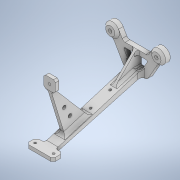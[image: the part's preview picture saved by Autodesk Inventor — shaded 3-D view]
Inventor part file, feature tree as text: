
AUTODESK INVENTOR PART (.ipt)
format: ipt  version: 2020 (Build 240168000, 168)  size: 514,560 bytes
history: native  units: mm
features: extrude x16, sketch x15, projected_geometry x15, fillet x13, reference x6, other x6, plane x3, chamfer x3, thicken_offset x2, mirror x1
ambient origin geometry x8: Origin, YZ Plane, XZ Plane, XY Plane, X Axis, Y Axis, Z Axis, Center Point
bodies: Solid1 (feature_tree)
feature tree (80):
  extrude  "Extrusion1"  Depth=12.0mm
  extrude  "Extrusion2"  Depth=4.0mm
  plane  "Work Plane1"
  extrude  "Extrusion3"  Depth=5.0mm
  extrude  "Extrusion4"  Depth=5.0mm
  sketch  "Sketch5"  dims[d7=10.0mm d8=0.0mm d9=5.0mm]
  plane  "Work Plane2"
  extrude  "Extrusion5"  Depth=2.0mm
  extrude  "Extrusion6"  Depth=4.0mm
  mirror  "Mirror1"
  extrude  "Extrusion7"  Depth=10.0mm TaperAngle=0.0deg
  extrude  "Extrusion8"  Depth=23.0mm
  extrude  "Extrusion9"  Depth=2.0mm
  plane  "Work Plane3"
  extrude  "Extrusion10"  Depth=3.0mm TaperAngle=0.0deg
  extrude  "Extrusion11"  Depth=6.0mm TaperAngle=0.0deg
  fillet  "Fillet1"  Radius=4.0mm
  fillet  "Fillet2"  Radius=4.0mm
  fillet  "Fillet3"  Radius=6.0mm
  chamfer  "Chamfer2"  Distance=2.0mm
  chamfer  "Chamfer3"  Distance=2.0mm
  fillet  "Fillet4"  Radius=5.0mm
  extrude  "Extrusion12"  Depth=3.0mm
  thicken_offset  "Thicken1"
  thicken_offset  "Thicken2"
  fillet  "Fillet5"  Radius=10.0mm
  fillet  "Fillet6"  Radius=10.0mm
  fillet  "Fillet7"  Radius=20.0mm
  fillet  "Fillet8"  Radius=3.0mm
  fillet  "Fillet9"  Radius=2.0mm
  fillet  "Fillet10"  Radius=3.0mm
  fillet  "Fillet11"  Radius=3.0mm
  fillet  "Fillet12"  Radius=2.0mm
  fillet  "Fillet13"  Radius=2.0mm
  extrude  "Extrusion13"  Depth=2.0mm
  extrude  "Extrusion14"  Depth=10.0mm
  extrude  "Extrusion15"  Depth=2.0mm
  extrude  "Extrusion16"  Depth=3.0mm TaperAngle=0.0deg
  chamfer  "Chamfer4"  Distance=2.0mm
  reference  "Reference1"
  reference  "Reference2"
  sketch  "Sketch2"  dims[d0=12.0mm d1=12.0mm]
  projected_geometry  "Projected Loop1"
  projected_geometry  "Projected Loop2"
  sketch  "Sketch3"  dims[d2=4.0mm d3=0.0mm d4=20.0mm]
  reference  "Reference3"
  sketch  "Sketch4"  dims[d5=5.0mm d6=20.0mm]
  reference  "Reference4"
  projected_geometry  "Projected Loop3"
  projected_geometry  "Projected Loop4"
  projected_geometry  "Projected Loop5"
  sketch  "Sketch6"  dims[d10=2.0mm d11=7.0mm]
  projected_geometry  "Projected Loop6"
  sketch  "Sketch7"  dims[d12=4.0mm d13=11.0mm]
  projected_geometry  "Projected Loop7"
  sketch  "Sketch8"  dims[d14=3.0mm d15=10.0mm d16=0.0mm]
  projected_geometry  "Projected Loop8"
  projected_geometry  "Projected Loop9"
  sketch  "Sketch9"  dims[d17=8.0mm d18=23.0mm]
  projected_geometry  "Projected Loop10"
  sketch  "Sketch10"  dims[d19=2.0mm d20=2.0mm]
  reference  "Reference5"
  sketch  "Sketch11"  dims[d21=3.0mm d22=0.0mm d23=3.0mm d24=0.0mm]
  projected_geometry  "Projected Loop11"
  projected_geometry  "Projected Loop12"
  sketch  "Sketch12"  dims[d25=12.0mm d26=6.0mm d27=0.0mm d28=4.0mm d29=4.0mm d30=6.0mm d31=0.0mm]
  projected_geometry  "Projected Loop13"
  sketch  "Sketch13"  dims[d32=13.5mm]
  reference  "Reference6"
  sketch  "Sketch14"  dims[d33=20.0mm d34=2.0mm d35=0.0mm d36=2.0mm d37=0.0mm d38=5.0mm]
  projected_geometry  "Projected Loop14"
  sketch  "Sketch15"  dims[d39=5.0mm d40=3.0mm d41=10.0mm d42=10.0mm d43=0.0mm d44=20.0mm d45=3.0mm d46=0.0mm d47=2.0mm d48=3.0mm d49=3.0mm]
  projected_geometry  "Projected Loop15"
  sketch  "Sketch16"  dims[d53=1.5mm d54=2.0mm d55=45.0deg d56=2.0mm d57=2.0mm d58=45.0deg d59=2.0mm d60=3.1mm d61=10.0mm d62=3.1mm d63=3.0mm d64=0.0mm d65=2.0mm d66=2.0mm d67=2.0mm d68=2.0mm d69=3.0mm d70=3.0mm d71=3.0mm d72=1.0mm d73=3.0mm d74=1.0mm d75=2.0mm d76=3.0mm d77=3.0mm d78=2.0mm d79=3.0mm d80=0.0mm d81=3.0mm d82=3.0mm d83=2.0mm d84=2.0mm d85=6.0mm d86=0.0mm d87=8.0mm d88=8.0mm d89=2.0mm d90=0.0mm d91=3.0mm d92=3.0mm d93=8.0mm d94=0.0mm d95=2.0mm d96=2.0mm d97=45.0deg]
  parser-record x1  (decoder bookkeeping rows leaked as tree rows — omitted from the tree; the rows remain in map.json)
  other  "body_1.iam"
  other  "body_conn_2:1"
  other  "body_conn_2_MIR:1"
  other  "body_shell_1:1"
  other  "body_shell_2:1"
note: 1 file-system path scrubbed to <path> (originals preserved in map.json)
